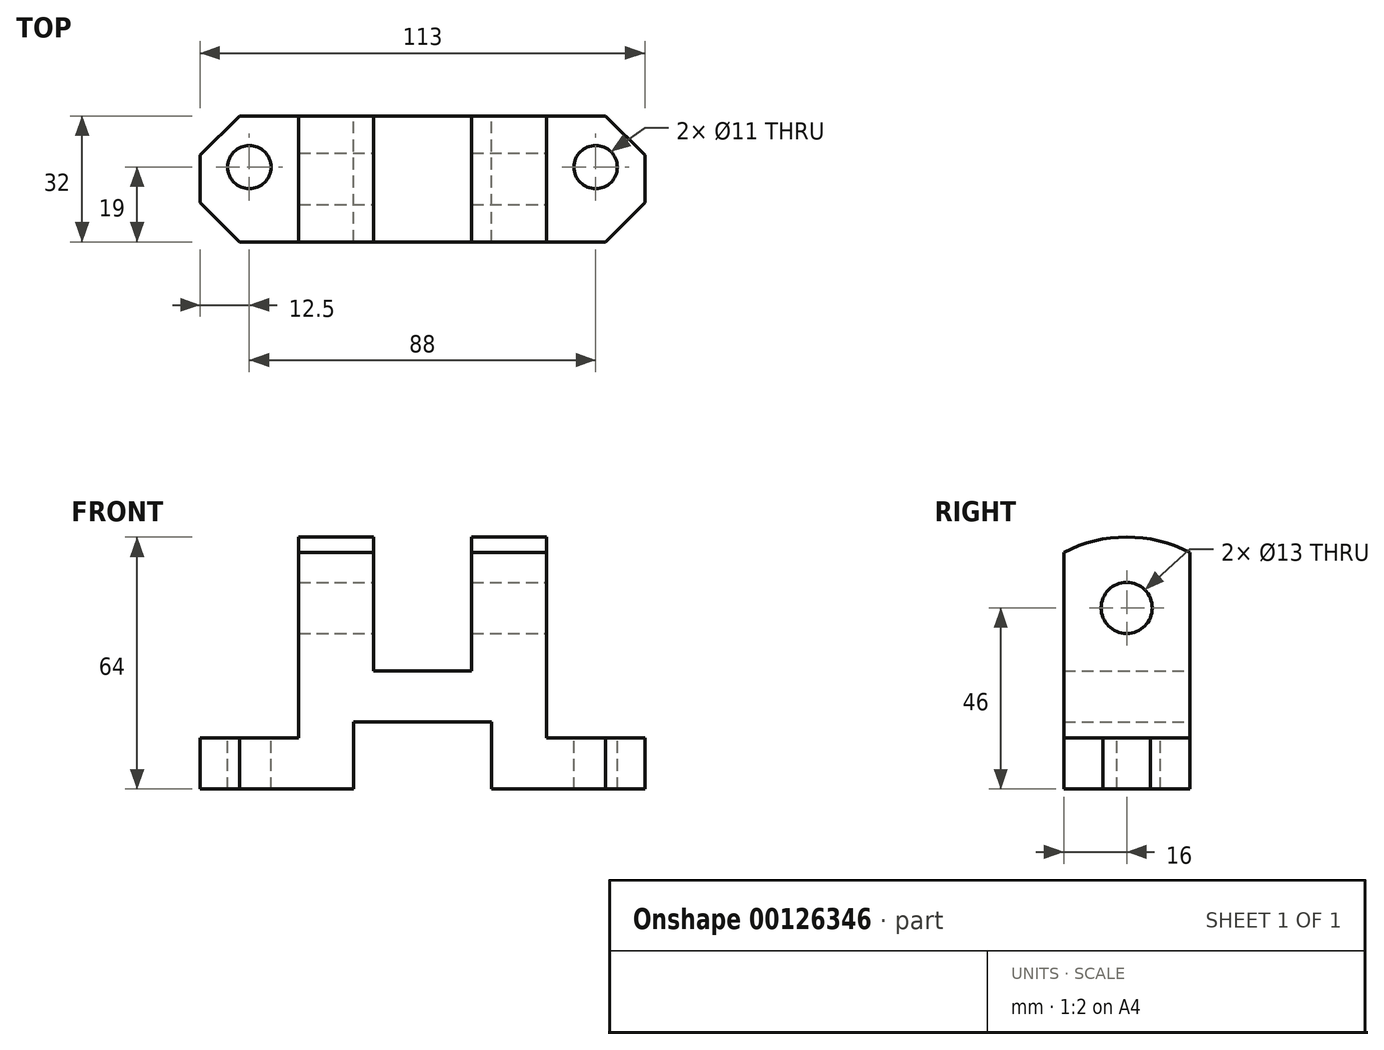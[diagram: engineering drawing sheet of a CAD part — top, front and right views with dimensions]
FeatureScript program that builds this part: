
annotation { "Feature Type Name" : "Feature", "Feature Type Description" : "" }
export const myFeature = defineFeature(function(context is Context, id is Id, definition is map)
    precondition{}
    {
        {
            var Q0;
            Q0=qCreatedBy(makeId("Front.planeOp"),FACE);
            var sketch = newSketch(context, id + "F0", { "sketchPlane" : qUnion([Q0])});
            skLineSegment(sketch, "E0", {"start": v(-39, 0) * mm, "end": v(-39, 13) * mm});
            skLineSegment(sketch, "E1", {"start": v(74, 13) * mm, "end": v(49, 13) * mm});
            skLineSegment(sketch, "E2", {"start": v(49, 13) * mm, "end": v(49, 60.13) * mm});
            skLineSegment(sketch, "E3", {"start": v(49, 60.13) * mm, "end": v(30, 60.13) * mm});
            skLineSegment(sketch, "E4", {"start": v(30, 60.13) * mm, "end": v(30, 30) * mm});
            skLineSegment(sketch, "E5", {"start": v(30, 30) * mm, "end": v(5, 30) * mm});
            skLineSegment(sketch, "E6", {"start": v(5, 30) * mm, "end": v(5, 60.13) * mm});
            skLineSegment(sketch, "E7", {"start": v(5, 60.13) * mm, "end": v(-14, 60.13) * mm});
            skLineSegment(sketch, "E8", {"start": v(-14, 60.13) * mm, "end": v(-14, 13) * mm});
            skLineSegment(sketch, "E9", {"start": v(-14, 13) * mm, "end": v(-39, 13) * mm});
            skLineSegment(sketch, "E10", {"start": v(74, 0) * mm, "end": v(74, 13) * mm});
            skLineSegment(sketch, "E11", {"start": v(-39, 0) * mm, "end": v(0, 0) * mm});
            skLineSegment(sketch, "E12", {"start": v(0, 0) * mm, "end": v(0, 17) * mm});
            skLineSegment(sketch, "E13", {"start": v(0, 17) * mm, "end": v(35, 17) * mm});
            skLineSegment(sketch, "E14", {"start": v(35, 17) * mm, "end": v(35, 0) * mm});
            skLineSegment(sketch, "E15", {"start": v(35, 0) * mm, "end": v(74, 0) * mm});
            skSolve(sketch);
        }
        {
            var Q0;
            Q0 = qSketchRegion(id + "F0", true);
            extrude(context, id + "F1", {"entities" : qUnion([Q0]), "depth" : 32 * mm});
        }
        {
            var Q0;
            Q0=makeQuery(id+"F1.opExtrude","SWEPT_FACE",FACE,{"disambiguationData":[OSD([sQuery(id+"F0.wireOp",EDGE,"E9")])]});
            var sketch = newSketch(context, id + "F2", { "sketchPlane" : qUnion([Q0])});
            skLineSegment(sketch, "E16", {"start": v(-29, -32) * mm, "end": v(-39, -22) * mm});
            skLineSegment(sketch, "E17", {"start": v(-39, -10) * mm, "end": v(-29, 0) * mm});
            skSolve(sketch);
        }
        {
            var Q0;
            Q0 = qSketchRegion(id + "F2", true);
            var Q1;
            {var subQ0=sQuery(id+"F2.wireOp",EDGE,"E16");Q1=makeQuery(id+"F2.imprint","IMPRINT",FACE,{"disambiguationData":[TD([[makeQuery(id+"F2.imprint","IMPRINT",EDGE,{"derivedFrom":subQ0}),1.0]])]});}
            var Q2;
            {var subQ0=sQuery(id+"F2.wireOp",EDGE,"E17");Q2=makeQuery(id+"F2.imprint","IMPRINT",FACE,{"disambiguationData":[TD([[makeQuery(id+"F2.imprint","IMPRINT",EDGE,{"derivedFrom":subQ0}),1.0]])]});}
            extrude(context, id + "F3", {"entities" : qUnion([Q0, Q1, Q2]), "operationType" : NewBodyOperationType.REMOVE, "oppositeDirection" : true, "depth" : 25 * mm});
        }
        {
            var Q0;
            Q0=makeQuery(id+"F1.opExtrude","SWEPT_FACE",FACE,{"disambiguationData":[OSD([sQuery(id+"F0.wireOp",EDGE,"E1")])]});
            var sketch = newSketch(context, id + "F4", { "sketchPlane" : qUnion([Q0])});
            skLineSegment(sketch, "E18", {"start": v(64, -32) * mm, "end": v(74, -22) * mm});
            skLineSegment(sketch, "E19", {"start": v(64, 0) * mm, "end": v(74, -10) * mm});
            skCircle(sketch, "E20", {"center": v(61.5, -13) * mm, "radius": 5.5 * mm});
            skSolve(sketch);
        }
        {
            var Q0;
            Q0 = qSketchRegion(id + "F4", true);
            var Q1;
            {var subQ0=sQuery(id+"F4.wireOp",EDGE,"E18");Q1=makeQuery(id+"F4.imprint","IMPRINT",FACE,{"disambiguationData":[TD([[makeQuery(id+"F4.imprint","IMPRINT",EDGE,{"derivedFrom":subQ0}),-1.0]])]});}
            var Q2;
            {var subQ0=sQuery(id+"F4.wireOp",EDGE,"E19");Q2=makeQuery(id+"F4.imprint","IMPRINT",FACE,{"disambiguationData":[TD([[makeQuery(id+"F4.imprint","IMPRINT",EDGE,{"derivedFrom":subQ0}),1.0]])]});}
            extrude(context, id + "F5", {"entities" : qUnion([Q0, Q1, Q2]), "operationType" : NewBodyOperationType.REMOVE, "oppositeDirection" : true, "depth" : 25 * mm});
        }
        {
            var Q0;
            Q0=makeQuery(id+"F1.opExtrude","SWEPT_FACE",FACE,{"disambiguationData":[OSD([sQuery(id+"F0.wireOp",EDGE,"E9")])]});
            var sketch = newSketch(context, id + "F6", { "sketchPlane" : qUnion([Q0])});
            skCircle(sketch, "E21", {"center": v(-26.5, -13) * mm, "radius": 5.5 * mm});
            skSolve(sketch);
        }
        {
            var Q0;
            Q0 = qSketchRegion(id + "F6", true);
            extrude(context, id + "F7", {"entities" : qUnion([Q0]), "operationType" : NewBodyOperationType.REMOVE, "oppositeDirection" : true, "depth" : 25 * mm});
        }
        {
            var Q0;
            Q0=makeQuery(id+"F1.opExtrude","SWEPT_FACE",FACE,{"disambiguationData":[OSD([sQuery(id+"F0.wireOp",EDGE,"E2")])]});
            var sketch = newSketch(context, id + "F8", { "sketchPlane" : qUnion([Q0])});
            skCircle(sketch, "E22", {"center": v(-16, 46) * mm, "radius": 6.5 * mm});
            skSolve(sketch);
        }
        {
            var Q0;
            Q0=makeQuery(id+"F8.imprint","IMPRINT",FACE,{"disambiguationData":[TD([[makeQuery(id+"F8.imprint","IMPRINT",EDGE,{"derivedFrom":sQuery(id+"F8.wireOp",EDGE,"E22")}),-1.0]])]});
            var sketch = newSketch(context, id + "F9", { "sketchPlane" : qUnion([Q0])});
            skArc(sketch, "E23", {"start": v(0, 60.13) * mm, "mid": v(-16, 64) * mm, "end": v(-32, 60.13) * mm});
            skSolve(sketch);
        }
        {
            var Q0;
            Q0=makeQuery(id+"F9.imprint","IMPRINT",FACE,{"disambiguationData":[TD([[makeQuery(id+"F9.imprint","IMPRINT",EDGE,{"derivedFrom":sQuery(id+"F9.wireOp",EDGE,"E23")}),1.0]])]});
            extrude(context, id + "F10", {"entities" : qUnion([Q0]), "operationType" : NewBodyOperationType.ADD, "oppositeDirection" : true, "depth" : 19 * mm});
        }
        {
            var Q0;
            Q0 = qSketchRegion(id + "F8", true);
            extrude(context, id + "F11", {"entities" : qUnion([Q0]), "operationType" : NewBodyOperationType.REMOVE, "endBound" : BoundingType.THROUGH_ALL, "oppositeDirection" : true, "depth" : 25 * mm});
        }
        {
            var Q0;
            Q0=makeQuery(id+"F1.opExtrude","SWEPT_FACE",FACE,{"disambiguationData":[OSD([sQuery(id+"F0.wireOp",EDGE,"E8")])]});
            var sketch = newSketch(context, id + "F12", { "sketchPlane" : qUnion([Q0])});
            skArc(sketch, "E24", {"start": v(32, 60.13) * mm, "mid": v(16, 64) * mm, "end": v(0, 60.13) * mm});
            skLineSegment(sketch, "E25", {"start": v(0, 60.13) * mm, "end": v(32, 60.13) * mm});
            skSolve(sketch);
        }
        {
            var Q0;
            Q0 = qSketchRegion(id + "F12", true);
            extrude(context, id + "F13", {"entities" : qUnion([Q0]), "operationType" : NewBodyOperationType.ADD, "oppositeDirection" : true, "depth" : 19 * mm});
        }
    });
